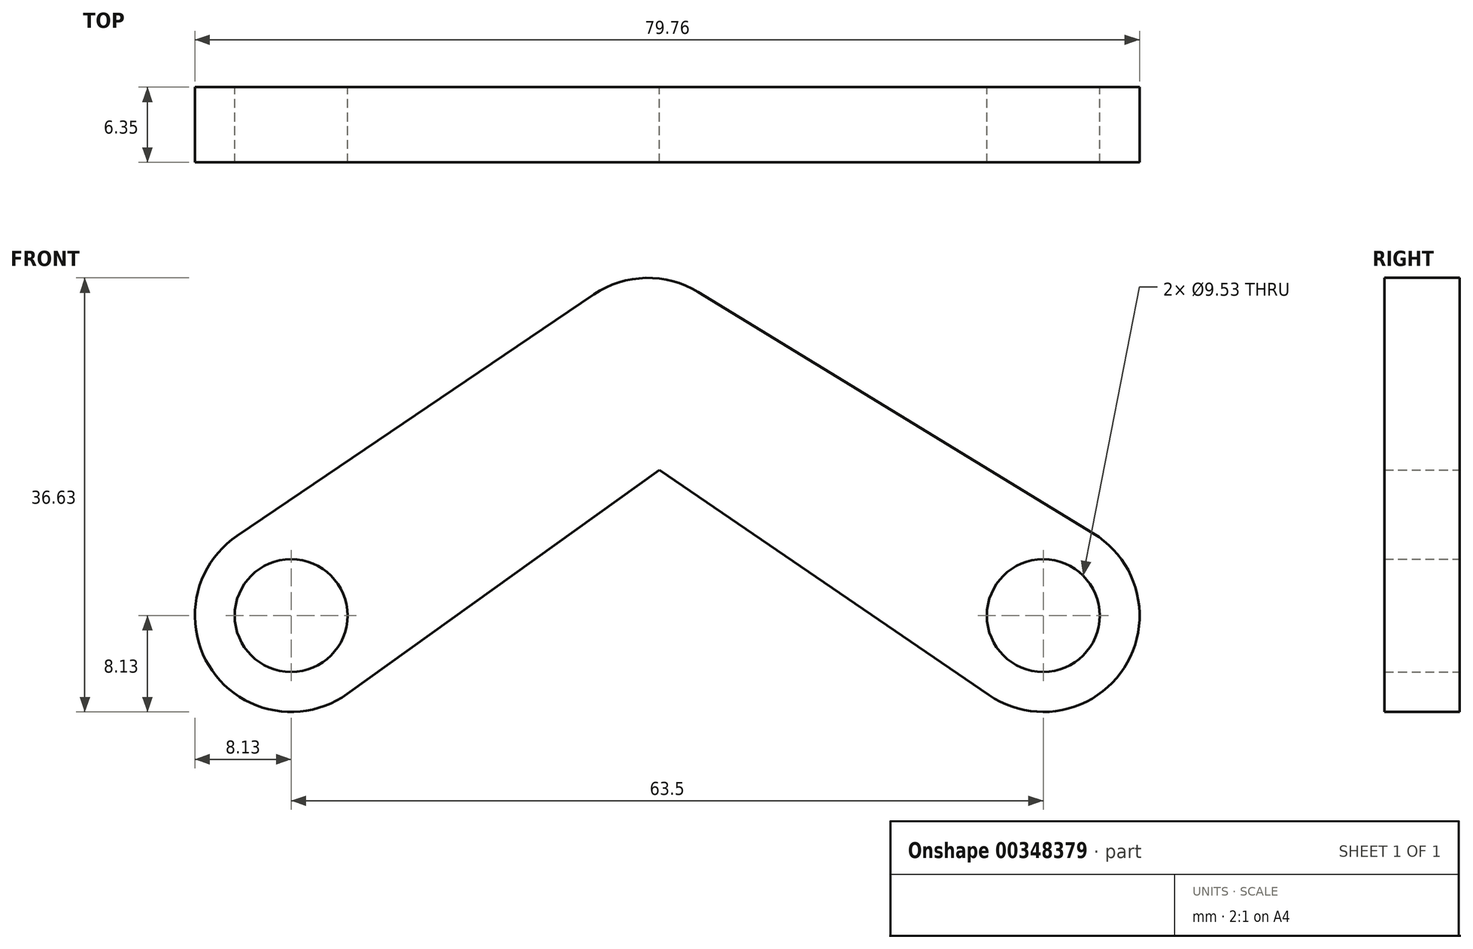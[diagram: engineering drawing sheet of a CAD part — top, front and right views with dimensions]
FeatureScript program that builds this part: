
annotation { "Feature Type Name" : "Feature", "Feature Type Description" : "" }
export const myFeature = defineFeature(function(context is Context, id is Id, definition is map)
    precondition{}
    {
        {
            var Q0;
            Q0=qCreatedBy(makeId("Front.planeOp"),FACE);
            var sketch = newSketch(context, id + "F0", { "sketchPlane" : qUnion([Q0])});
            skCircle(sketch, "E0", {"center": v(0, 0) * mm, "radius": 4.76 * mm});
            skCircle(sketch, "E1", {"center": v(63.5, 0) * mm, "radius": 4.76 * mm});
            skCircle(sketch, "E2", {"center": v(0, 0) * mm, "radius": 8.13 * mm});
            skCircle(sketch, "E3", {"center": v(63.5, 0) * mm, "radius": 8.13 * mm});
            skCircle(sketch, "E4", {"center": v(30.13, 20.37) * mm, "radius": 4.76 * mm});
            skCircle(sketch, "E5", {"center": v(30.13, 20.37) * mm, "radius": 8.13 * mm});
            skLineSegment(sketch, "E6", {"start": v(-4.55, 6.73) * mm, "end": v(25.58, 27.1) * mm});
            skLineSegment(sketch, "E7", {"start": v(34.36, 27.3) * mm, "end": v(67.74, 6.94) * mm});
            skLineSegment(sketch, "E8", {"start": v(4.74, -6.6) * mm, "end": v(31.08, 12.3) * mm});
            skLineSegment(sketch, "E9", {"start": v(31.08, 12.3) * mm, "end": v(58.92, -6.71) * mm});
            skSolve(sketch);
        }
        {
            var Q0;
            Q0=makeQuery(id+"F0.imprint","IMPRINT",FACE,{"disambiguationData":[TD([[makeQuery(id+"F0.imprint","IMPRINT",EDGE,{"derivedFrom":sQuery(id+"F0.wireOp",EDGE,"E0")}),-1.0]])]});
            var Q1;
            {var subQ0=sQuery(id+"F0.wireOp",EDGE,"E6");Q1=makeQuery(id+"F0.imprint","IMPRINT",FACE,{"disambiguationData":[TD([[makeQuery(id+"F0.imprint","IMPRINT",EDGE,{"derivedFrom":subQ0}),-1.0]])]});}
            var Q2;
            Q2=makeQuery(id+"F0.imprint","IMPRINT",FACE,{"disambiguationData":[TD([[makeQuery(id+"F0.imprint","IMPRINT",EDGE,{"derivedFrom":sQuery(id+"F0.wireOp",EDGE,"E4")}),-1.0]])]});
            var Q3;
            Q3=makeQuery(id+"F0.imprint","IMPRINT",FACE,{"disambiguationData":[TD([[makeQuery(id+"F0.imprint","IMPRINT",EDGE,{"derivedFrom":sQuery(id+"F0.wireOp",EDGE,"E4")}),1.0]])]});
            var Q4;
            {var subQ0=sQuery(id+"F0.wireOp",EDGE,"E7");Q4=makeQuery(id+"F0.imprint","IMPRINT",FACE,{"disambiguationData":[TD([[makeQuery(id+"F0.imprint","IMPRINT",EDGE,{"derivedFrom":subQ0}),-1.0]])]});}
            var Q5;
            Q5=makeQuery(id+"F0.imprint","IMPRINT",FACE,{"disambiguationData":[TD([[makeQuery(id+"F0.imprint","IMPRINT",EDGE,{"derivedFrom":sQuery(id+"F0.wireOp",EDGE,"E1")}),-1.0]])]});
            extrude(context, id + "F1", {"entities" : qUnion([Q0, Q1, Q2, Q3, Q4, Q5]), "depth" : 6.35 * mm});
        }
    });
